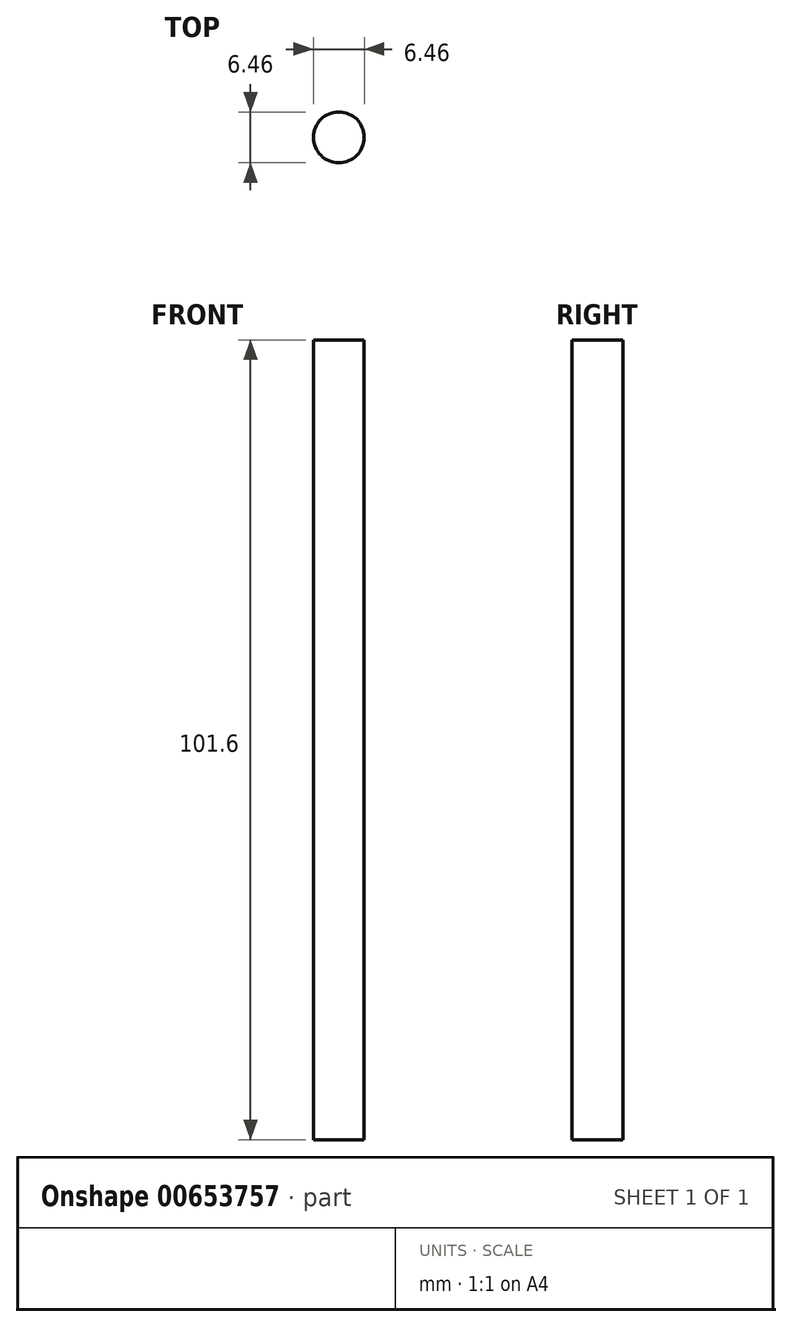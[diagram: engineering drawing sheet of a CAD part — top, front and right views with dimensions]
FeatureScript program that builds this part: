
annotation { "Feature Type Name" : "Feature", "Feature Type Description" : "" }
export const myFeature = defineFeature(function(context is Context, id is Id, definition is map)
    precondition{}
    {
        {
            var Q0;
            Q0=qCreatedBy(makeId("Top.planeOp"),FACE);
            var sketch = newSketch(context, id + "F0", { "sketchPlane" : qUnion([Q0])});
            skCircle(sketch, "E0", {"center": v(0, 0) * mm, "radius": 3.23 * mm});
            skSolve(sketch);
        }
        {
            var Q0;
            Q0 = qSketchRegion(id + "F0", true);
            extrude(context, id + "F1", {"entities" : qUnion([Q0]), "depth" : 101.6 * mm, "offsetDistance" : 25.4 * mm});
        }
    });
